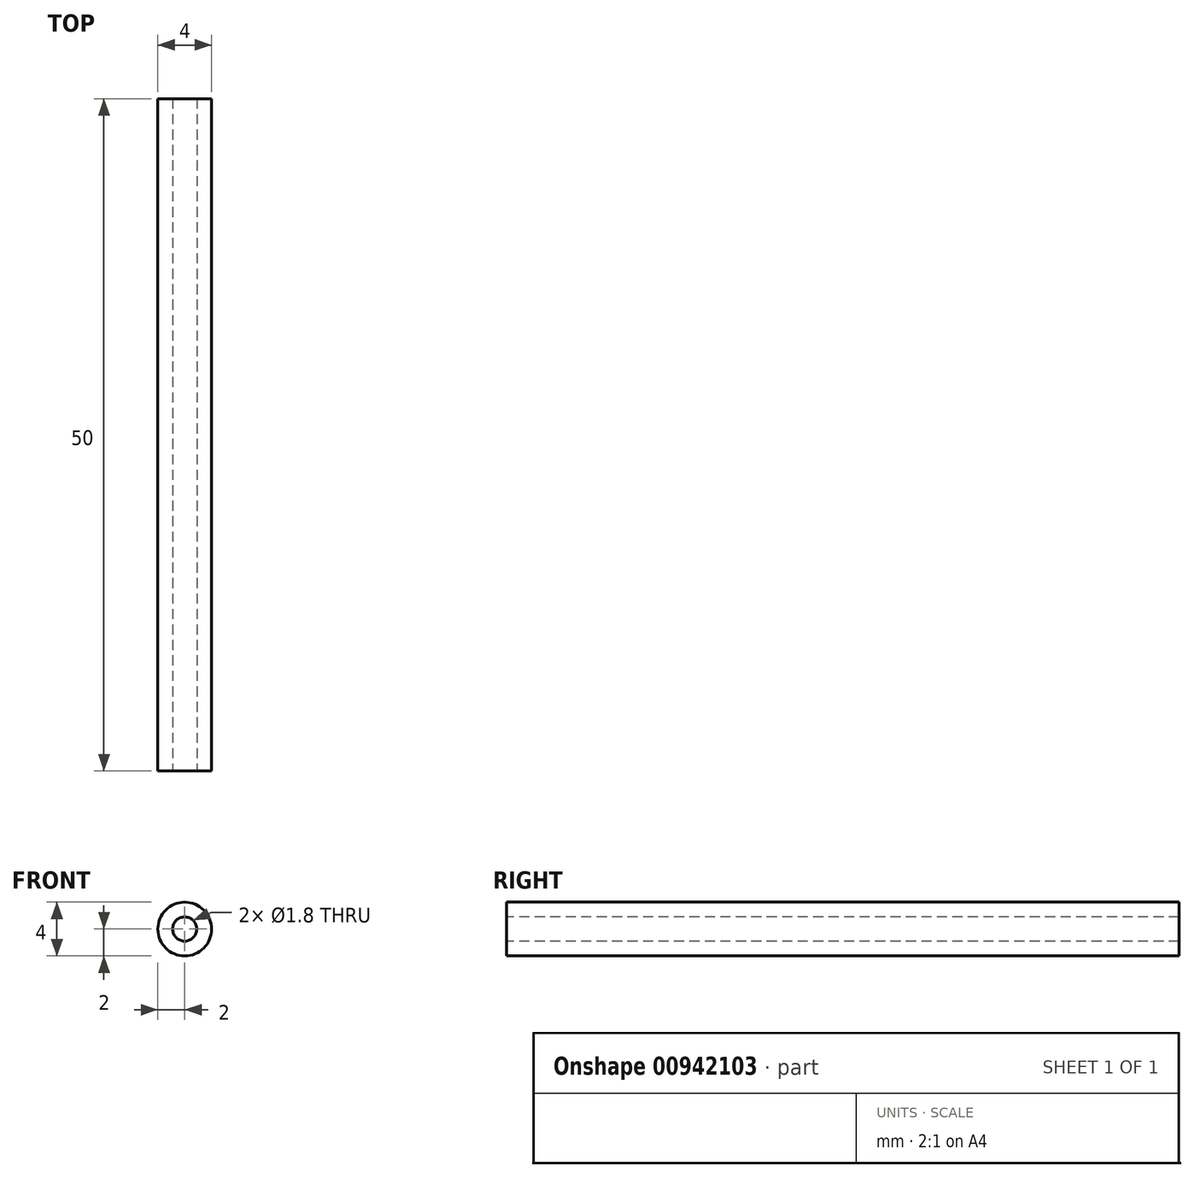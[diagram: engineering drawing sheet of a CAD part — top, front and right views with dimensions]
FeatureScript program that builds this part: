
annotation { "Feature Type Name" : "Feature", "Feature Type Description" : "" }
export const myFeature = defineFeature(function(context is Context, id is Id, definition is map)
    precondition{}
    {
        {
            var Q0;
            Q0=qCreatedBy(makeId("Front.planeOp"),FACE);
            var sketch = newSketch(context, id + "F0", { "sketchPlane" : qUnion([Q0])});
            skCircle(sketch, "E0", {"center": v(0, 0) * mm, "radius": 2 * mm});
            skCircle(sketch, "E1", {"center": v(0, 0) * mm, "radius": 0.9 * mm});
            skSolve(sketch);
        }
        {
            var Q0;
            Q0 = qSketchRegion(id + "F0", true);
            extrude(context, id + "F1", {"entities" : qUnion([Q0]), "oppositeDirection" : true, "depth" : 50 * mm, "offsetDistance" : 25 * mm});
        }
    });
